# Revit family: NLRS_57_DUA_UN_roof_kerb_for_penthouse_louvre_bdon_LT_sacs
name_source: partatom
category: Duct Accessories
units: mm (PartAtom-declared; Revit-internal decimal feet)

## family parameters
Always vertical = Yes
Cut with Voids When Loaded = No
Part Type = Attaches To
Round Connector Dimension = Use Diameter
Shared = Yes
Work Plane-Based = No

## types (4) — shared parameters
Assembly Code = 57.0
LookupTable = BDON
Manufacturer = Solid Air Climate Solutions
Model = Solid Air roof curb, BDON
NLRS_C_content_datum_uitgifte = 21-04-2023
NLRS_C_content_provider = Solid Air Climate Solutions
NLRS_C_content_versie = 3.20.02
NLRS_C_niveau ontwikkeling = LOD 400
zero-valued in all types: Default Elevation

## per-type parameters (varying)
| type | Description | NLRS_C_description | SACS_Base_Index | SACS_Face_Color | SACS_Frame_1 | SACS_Frame_2 | SACS_Material |
| BDONOD | Galvanised steel roof curb, non-insulated | Galvanised steel roof curb, non-insulated | 1 | NLRS_57_sendzimir verzinkt_gen_sacs | Yes | No | galvanised steel |
| BDONOR | Galvanised steel roof curb, insulated | Galvanised steel roof curb, insulated | 2 | NLRS_57_sendzimir verzinkt_gen_sacs | No | Yes | galvanised steel |
| BDONAD | Aluminum roof curb, non-insulated | Aluminum roof curb, non-insulated | 3 | NLRS_57_aluminium_gen_sacs | Yes | No | seawater proof aluminium |
| BDONAR | Aluminum roof curb, insulated | Aluminum roof curb, insulated | 4 | NLRS_57_aluminium_gen_sacs | No | Yes | seawater proof aluminium |

## geometry (parser evidence)
native form markers: Sweep x6
no freeform markers — native parametric forms only
